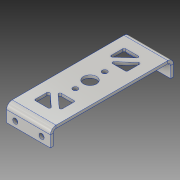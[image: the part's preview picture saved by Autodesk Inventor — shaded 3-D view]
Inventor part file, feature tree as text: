
AUTODESK INVENTOR PART (.ipt)
format: ipt  version: 2016 SP1 (Build 200210100, 210)  size: 184,832 bytes
history: native  units: in
note: dims shown in document units (in); Inventor stores cm internally (conversion verified against a paired STEP export)
features: sheet_metal_op x4, sketch x4, other x3, hole x1
ambient origin geometry x8: Origin, YZ Plane, XZ Plane, XY Plane, X Axis, Y Axis, Z Axis, Center Point
bodies: Solid1 (feature_tree)
feature tree (12):
  sheet_metal_op  "Face1"
  sheet_metal_op  "Flange1"
  hole  "Hole1"  [1 undecoded]
  sketch  "Sketch1"  dims[d0=1.0in d1=2.808in]
  other  "Plate1"
  sketch  "Sketch2"  dims[d2=0.0641in]
  other  "Plate2"
  sheet_metal_op  "Bend1"
  sheet_metal_op  "Corner1"
  sketch  "Sketch3"  dims[d3=0.0641in]
  sketch  "Sketch4"  dims[d4=0.0321in d5=0.1282in d6=0.0641in d7=0.387in d8=90.0deg d9=0.0641in d10=0.2564in d11=0.0641in d12=0.0641in d28=0.0312in d29=0.375in d30=0.819in d32=0.67in d34=1.069in d35=1.739in d36=1.989in d37=2.433in d38=0.525in d39=0.25in d40=1.404in d41=2.138in d42=2.283in d43=0.2812in d44=0.43in d45=0.5in d46=0.57in d47=0.719in d48=0.7502in d49=1.0in d50=0.3in d51=0.0641in d52=0.0in d53=0.2in d54=0.8in d55=0.256in d56=0.116in d57=0.75in d58=0.375in d59=0.25in d60=0.5635in d61=0.0641in d62=0.8108in]
  other  "Cut1"
note: 1 required parameter value undecoded (feature->parameter linkage not recoverable at this tier; creation-order binding heuristic only, values carry confidence <= 0.55)
